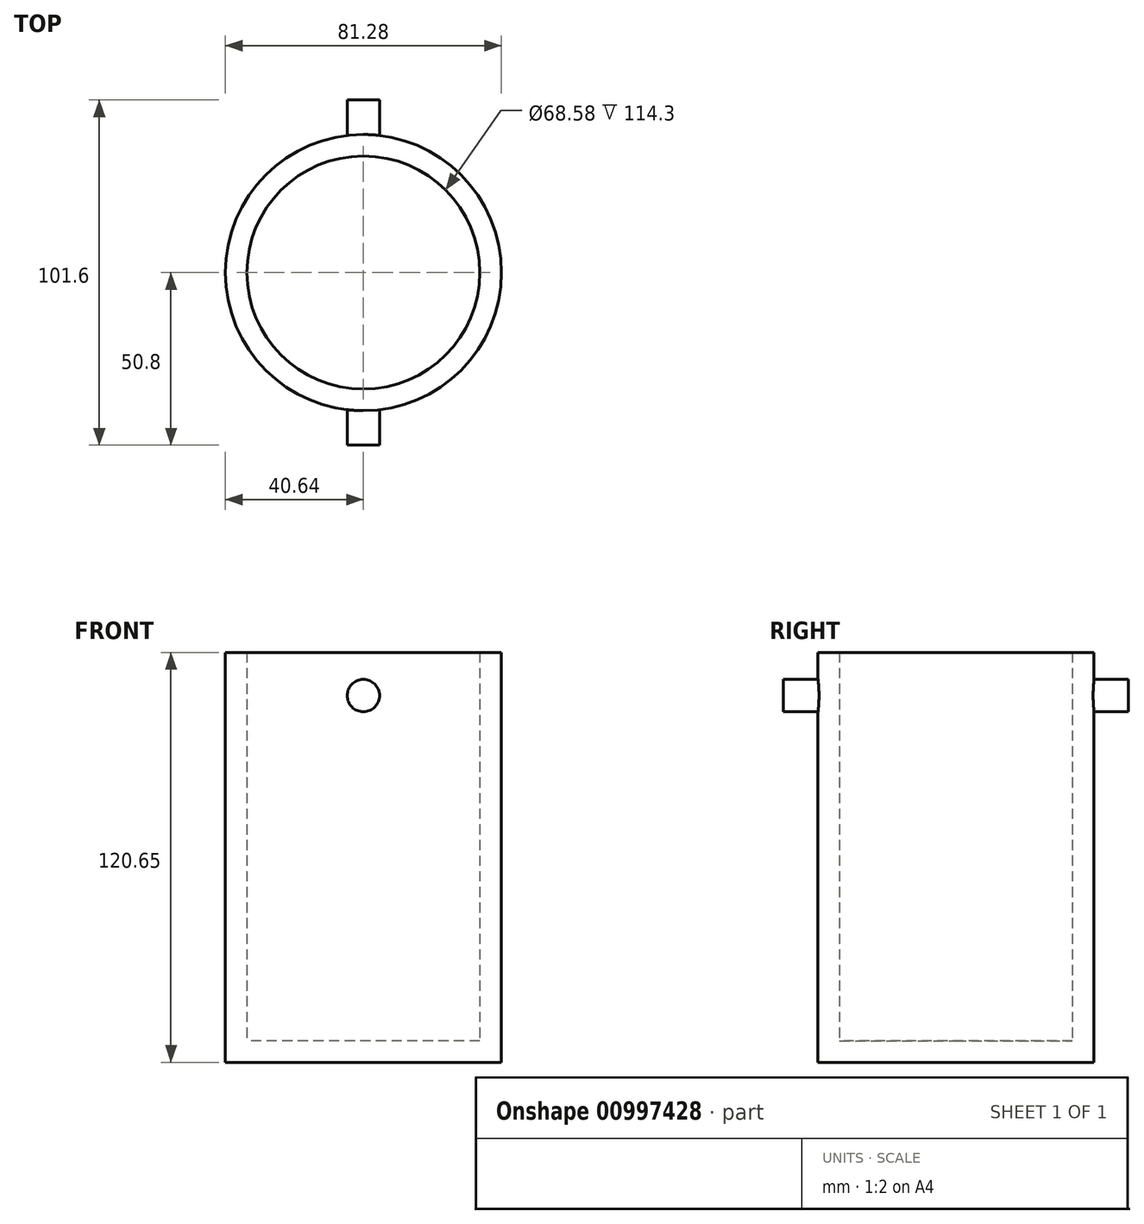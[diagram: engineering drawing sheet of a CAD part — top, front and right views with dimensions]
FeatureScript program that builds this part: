
annotation { "Feature Type Name" : "Feature", "Feature Type Description" : "" }
export const myFeature = defineFeature(function(context is Context, id is Id, definition is map)
    precondition{}
    {
        {
            var Q0;
            Q0=qCreatedBy(makeId("Top.planeOp"),FACE);
            var sketch = newSketch(context, id + "F0", { "sketchPlane" : qUnion([Q0])});
            skCircle(sketch, "E0", {"center": v(0, 0) * mm, "radius": 34.3 * mm});
            skCircle(sketch, "E1.0", {"center": v(0, 0) * mm, "radius": 40.64 * mm});
            skSolve(sketch);
        }
        {
            var Q0;
            Q0=makeQuery(id+"F0.imprint","IMPRINT",FACE,{"disambiguationData":[TD([[makeQuery(id+"F0.imprint","IMPRINT",EDGE,{"derivedFrom":sQuery(id+"F0.wireOp",EDGE,"E0")}),-1.0]])]});
            extrude(context, id + "F1", {"entities" : qUnion([Q0]), "depth" : 120.65 * mm, "offsetDistance" : 25.4 * mm});
        }
        {
            var Q0;
            Q0=makeQuery(id+"F0.imprint","IMPRINT",FACE,{"disambiguationData":[TD([[makeQuery(id+"F0.imprint","IMPRINT",EDGE,{"derivedFrom":sQuery(id+"F0.wireOp",EDGE,"E0")}),1.0]])]});
            extrude(context, id + "F2", {"entities" : qUnion([Q0]), "operationType" : NewBodyOperationType.ADD, "depth" : 6.35 * mm, "offsetDistance" : 25.4 * mm});
        }
        {
            var Q0;
            Q0=qCreatedBy(makeId("Front.planeOp"),FACE);
            var sketch = newSketch(context, id + "F3", { "sketchPlane" : qUnion([Q0])});
            skCircle(sketch, "E2", {"center": v(0, 107.95) * mm, "radius": 4.76 * mm});
            skSolve(sketch);
        }
        {
            var Q0;
            Q0 = qSketchRegion(id + "F3", true);
            var Q1;
            Q1=sQuery(id+"F3.wireOp",EDGE,"E2");
            extrude(context, id + "F4", {"entities" : qUnion([Q0]), "operationType" : NewBodyOperationType.ADD, "surfaceEntities" : qUnion([Q1]), "depth" : 50.8 * mm, "offsetDistance" : 25.4 * mm, "hasSecondDirection" : true, "secondDirectionOppositeDirection" : true, "secondDirectionDepth" : 50.8 * mm});
        }
        {
            var Q0;
            Q0=makeQuery(id+"F2.opExtrude","CAP_FACE",FACE,{"disambiguationData":[OSD([sQuery(id+"F0.wireOp",EDGE,"E0")])],"isStart":false});
            extrude(context, id + "F5", {"entities" : qUnion([Q0]), "operationType" : NewBodyOperationType.REMOVE, "endBound" : BoundingType.THROUGH_ALL, "depth" : 25.4 * mm, "offsetDistance" : 25.4 * mm});
        }
    });
